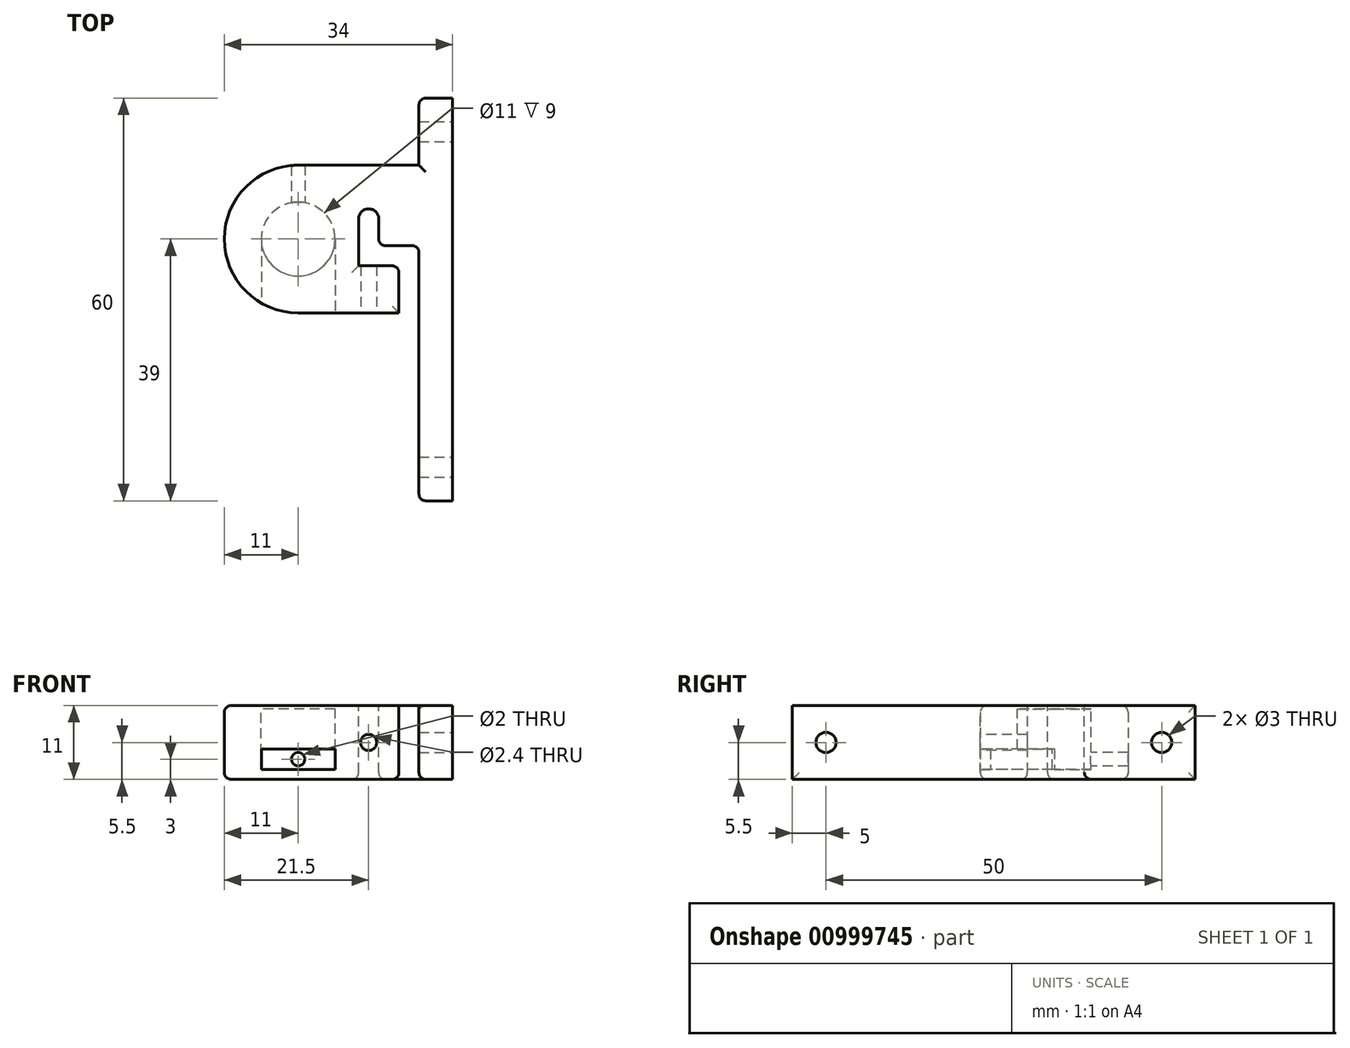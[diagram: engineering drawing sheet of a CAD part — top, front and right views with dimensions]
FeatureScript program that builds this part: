
annotation { "Feature Type Name" : "Feature", "Feature Type Description" : "" }
export const myFeature = defineFeature(function(context is Context, id is Id, definition is map)
    precondition{}
    {
        {
            var Q0;
            Q0=qCreatedBy(makeId("Top.planeOp"),FACE);
            var sketch = newSketch(context, id + "F0", { "sketchPlane" : qUnion([Q0])});
            skArc(sketch, "E0", {"start": v(0, 11) * mm, "mid": v(-11, 0) * mm, "end": v(0, -11) * mm});
            skLineSegment(sketch, "E1.bottom", {"start": v(23, -39) * mm, "end": v(18, -39) * mm});
            skLineSegment(sketch, "E1.top", {"start": v(23, 21) * mm, "end": v(18, 21) * mm});
            skLineSegment(sketch, "E1.left", {"start": v(23, -39) * mm, "end": v(23, 21) * mm});
            skLineSegment(sketch, "E1.right", {"start": v(18, -39) * mm, "end": v(18, -11) * mm});
            skLineSegment(sketch, "E2.bottom", {"start": v(0, 11) * mm, "end": v(18, 11) * mm});
            skLineSegment(sketch, "E2.top", {"start": v(0, -11) * mm, "end": v(18, -11) * mm});
            skLineSegment(sketch, "E3.trimOffspring", {"start": v(18, 11) * mm, "end": v(18, 21) * mm});
            skLineSegment(sketch, "E4", {"start": v(18, 11) * mm, "end": v(18, -11) * mm, "construction": true});
            skSolve(sketch);
        }
        {
            var Q0;
            Q0=qSketchRegion(id+"F0",true);
            extrude(context, id + "F1", {"entities" : qUnion([Q0]), "endBound" : BoundingType.SYMMETRIC, "depth" : 11 * mm, "offsetDistance" : 25 * mm});
        }
        {
            var Q0;
            Q0=makeQuery(id+"F1.opExtrude","SWEPT_FACE",FACE,{"disambiguationData":[OSD([sQuery(id+"F0.wireOp",EDGE,"E1.left")])]});
            var sketch = newSketch(context, id + "F2", { "sketchPlane" : qUnion([Q0])});
            skCircle(sketch, "E5", {"center": v(16, 0) * mm, "radius": 1.5 * mm});
            skCircle(sketch, "E6", {"center": v(-34, 0) * mm, "radius": 1.5 * mm});
            skSolve(sketch);
        }
        {
            var Q0;
            Q0=qSketchRegion(id+"F2",true);
            extrude(context, id + "F3", {"entities" : qUnion([Q0]), "operationType" : NewBodyOperationType.REMOVE, "oppositeDirection" : true, "depth" : 25 * mm, "offsetDistance" : 25 * mm});
        }
        {
            var Q0;
            Q0=makeQuery(id+"F1.opExtrude","CAP_FACE",FACE,{"disambiguationData":[OSD([sQuery(id+"F0.wireOp",EDGE,"E0"),sQuery(id+"F0.wireOp",EDGE,"E1.bottom"),sQuery(id+"F0.wireOp",EDGE,"E1.top"),sQuery(id+"F0.wireOp",EDGE,"E1.left"),sQuery(id+"F0.wireOp",EDGE,"E1.right"),sQuery(id+"F0.wireOp",EDGE,"E2.bottom"),sQuery(id+"F0.wireOp",EDGE,"E2.top"),sQuery(id+"F0.wireOp",EDGE,"E3.trimOffspring")])],"isStart":false});
            var sketch = newSketch(context, id + "F4", { "sketchPlane" : qUnion([Q0])});
            skCircle(sketch, "E7", {"center": v(0, 0) * mm, "radius": 5.5 * mm});
            skSolve(sketch);
        }
        {
            var Q0;
            Q0=makeQuery(id+"F4.imprint","IMPRINT",FACE,{"disambiguationData":[TD([[makeQuery(id+"F4.imprint","IMPRINT",EDGE,{"derivedFrom":sQuery(id+"F4.wireOp",EDGE,"E7")}),1.0]])]});
            extrude(context, id + "F5", {"entities" : qUnion([Q0]), "operationType" : NewBodyOperationType.REMOVE, "oppositeDirection" : true, "depth" : 9.5 * mm, "offsetDistance" : 25 * mm, "hasSecondDirection" : true, "secondDirectionOppositeDirection" : true, "secondDirectionDepth" : .5 * mm});
        }
        {
            var Q0;
            Q0=makeQuery(id+"F1.opExtrude","CAP_FACE",FACE,{"disambiguationData":[OSD([sQuery(id+"F0.wireOp",EDGE,"E0"),sQuery(id+"F0.wireOp",EDGE,"E1.bottom"),sQuery(id+"F0.wireOp",EDGE,"E1.top"),sQuery(id+"F0.wireOp",EDGE,"E1.left"),sQuery(id+"F0.wireOp",EDGE,"E1.right"),sQuery(id+"F0.wireOp",EDGE,"E2.bottom"),sQuery(id+"F0.wireOp",EDGE,"E2.top"),sQuery(id+"F0.wireOp",EDGE,"E3.trimOffspring")])],"isStart":true});
            var sketch = newSketch(context, id + "F6", { "sketchPlane" : qUnion([Q0])});
            skLineSegment(sketch, "E8.bottom", {"start": v(-5.5, 0) * mm, "end": v(5.5, 0) * mm});
            skLineSegment(sketch, "E8.top", {"start": v(-5.5, 16.46) * mm, "end": v(5.5, 16.46) * mm});
            skLineSegment(sketch, "E8.left", {"start": v(-5.5, 0) * mm, "end": v(-5.5, 16.46) * mm});
            skLineSegment(sketch, "E8.right", {"start": v(5.5, 0) * mm, "end": v(5.5, 16.46) * mm});
            skSolve(sketch);
        }
        {
            var Q0;
            Q0=qSketchRegion(id+"F6",true);
            extrude(context, id + "F7", {"entities" : qUnion([Q0]), "operationType" : NewBodyOperationType.REMOVE, "oppositeDirection" : true, "depth" : 4.5 * mm, "offsetDistance" : 25 * mm, "hasSecondDirection" : true, "secondDirectionOppositeDirection" : true, "secondDirectionDepth" : 1.5 * mm});
        }
        {
            var Q0;
            Q0=makeQuery(id+"F1.opExtrude","SWEPT_FACE",FACE,{"disambiguationData":[OSD([sQuery(id+"F0.wireOp",EDGE,"E2.top")])]});
            var sketch = newSketch(context, id + "F8", { "sketchPlane" : qUnion([Q0])});
            skCircle(sketch, "E9", {"center": v(0, -2.5) * mm, "radius": 1 * mm});
            skPoint(sketch, "E9.centerSnap0", {"position": v(5.5, -2.5) * mm});
            skSolve(sketch);
        }
        {
            var Q0;
            Q0=qSketchRegion(id+"F8",true);
            extrude(context, id + "F9", {"entities" : qUnion([Q0]), "operationType" : NewBodyOperationType.REMOVE, "oppositeDirection" : true, "depth" : 25 * mm, "offsetDistance" : 25 * mm});
        }
        {
            var Q0;
            Q0=makeQuery(id+"F4.imprint","IMPRINT",FACE,{"disambiguationData":[TD([[makeQuery(id+"F4.imprint","IMPRINT",EDGE,{"derivedFrom":sQuery(id+"F4.wireOp",EDGE,"E7")}),-1.0]])]});
            var sketch = newSketch(context, id + "F10", { "sketchPlane" : qUnion([Q0])});
            skArc(sketch, "E10", {"start": v(12, 3) * mm, "mid": v(10.5, 4.5) * mm, "end": v(9, 3) * mm});
            skLineSegment(sketch, "E11", {"start": v(9, 3) * mm, "end": v(9, -4) * mm});
            skLineSegment(sketch, "E12", {"start": v(9, -4) * mm, "end": v(15, -4) * mm});
            skLineSegment(sketch, "E13", {"start": v(15, -4) * mm, "end": v(15, -11) * mm});
            skLineSegment(sketch, "E14", {"start": v(15, -11) * mm, "end": v(18, -11) * mm});
            skLineSegment(sketch, "E15", {"start": v(18, -11) * mm, "end": v(18, -1) * mm});
            skLineSegment(sketch, "E16", {"start": v(18, -1) * mm, "end": v(12, -1) * mm});
            skLineSegment(sketch, "E17", {"start": v(12, -1) * mm, "end": v(12, 3) * mm});
            skSolve(sketch);
        }
        {
            var Q0;
            Q0=qSketchRegion(id+"F10",true);
            extrude(context, id + "F11", {"entities" : qUnion([Q0]), "operationType" : NewBodyOperationType.REMOVE, "oppositeDirection" : true, "depth" : 25 * mm, "offsetDistance" : 25 * mm});
        }
        {
            var Q0;
            Q0=makeQuery(id+"F1.opExtrude","SWEPT_FACE",FACE,{"disambiguationData":[OSD([sQuery(id+"F0.wireOp",EDGE,"E2.top")])]});
            var sketch = newSketch(context, id + "F12", { "sketchPlane" : qUnion([Q0])});
            skCircle(sketch, "E18", {"center": v(10.5, 0) * mm, "radius": 1.2 * mm});
            skSolve(sketch);
        }
        {
            var Q0;
            Q0=qSketchRegion(id+"F12",true);
            extrude(context, id + "F13", {"entities" : qUnion([Q0]), "operationType" : NewBodyOperationType.REMOVE, "endBound" : BoundingType.UP_TO_NEXT, "oppositeDirection" : true, "depth" : 25 * mm, "offsetDistance" : 25 * mm});
        }
        {
            var Q0;
            Q0=makeQuery(id+"F1.opExtrude","CAP_EDGE",EDGE,{"disambiguationData":[OSD([sQuery(id+"F0.wireOp",EDGE,"E3.trimOffspring")])],"isStart":false});
            var Q1;
            Q1=makeQuery(id+"F1.opExtrude","SWEPT_EDGE",EDGE,{"disambiguationData":[OSD([sQuery(id+"F0.wireOp",EDGE,"E1.top"),sQuery(id+"F0.wireOp",EDGE,"E3.trimOffspring")])]});
            var Q2;
            Q2=makeQuery(id+"F1.opExtrude","CAP_EDGE",EDGE,{"disambiguationData":[OSD([sQuery(id+"F0.wireOp",EDGE,"E3.trimOffspring")])],"isStart":true});
            var Q3;
            Q3=makeQuery(id+"F1.opExtrude","CAP_EDGE",EDGE,{"disambiguationData":[OSD([sQuery(id+"F0.wireOp",EDGE,"E2.bottom")])],"isStart":false});
            var Q4;
            Q4=makeQuery(id+"F11.boolean.opBoolean","MERGE",EDGE,{"derivedFrom":[makeQuery(id+"F1.opExtrude","CAP_EDGE",EDGE,{"disambiguationData":[OSD([sQuery(id+"F0.wireOp",EDGE,"E1.right")])],"isStart":false})],"fromTools":[makeQuery(id+"F11.opExtrude","CAP_EDGE",EDGE,{"disambiguationData":[OSD([sQuery(id+"F10.wireOp",EDGE,"E15")])],"isStart":true})]});
            var Q5;
            Q5=makeQuery(id+"F1.opExtrude","CAP_EDGE",EDGE,{"disambiguationData":[OSD([sQuery(id+"F0.wireOp",EDGE,"E0")])],"isStart":true});
            var Q6;
            Q6=makeQuery(id+"F1.opExtrude","CAP_EDGE",EDGE,{"disambiguationData":[OSD([sQuery(id+"F0.wireOp",EDGE,"E2.top")])],"isStart":true});
            var Q7;
            Q7=makeQuery(id+"F11.boolean.opBoolean","INTERSECT",EDGE,{"derivedFrom":[makeQuery(id+"F1.opExtrude","CAP_FACE",FACE,{"disambiguationData":[OSD([sQuery(id+"F0.wireOp",EDGE,"E0"),sQuery(id+"F0.wireOp",EDGE,"E1.bottom"),sQuery(id+"F0.wireOp",EDGE,"E1.top"),sQuery(id+"F0.wireOp",EDGE,"E1.left"),sQuery(id+"F0.wireOp",EDGE,"E1.right"),sQuery(id+"F0.wireOp",EDGE,"E2.bottom"),sQuery(id+"F0.wireOp",EDGE,"E2.top"),sQuery(id+"F0.wireOp",EDGE,"E3.trimOffspring")])],"isStart":true}),makeQuery(id+"F11.opExtrude","SWEPT_FACE",FACE,{"disambiguationData":[OSD([sQuery(id+"F10.wireOp",EDGE,"E15")])]})]});
            var Q8;
            Q8=makeQuery(id+"F11.boolean.opBoolean","INTERSECT",EDGE,{"derivedFrom":[makeQuery(id+"F1.opExtrude","CAP_FACE",FACE,{"disambiguationData":[OSD([sQuery(id+"F0.wireOp",EDGE,"E0"),sQuery(id+"F0.wireOp",EDGE,"E1.bottom"),sQuery(id+"F0.wireOp",EDGE,"E1.top"),sQuery(id+"F0.wireOp",EDGE,"E1.left"),sQuery(id+"F0.wireOp",EDGE,"E1.right"),sQuery(id+"F0.wireOp",EDGE,"E2.bottom"),sQuery(id+"F0.wireOp",EDGE,"E2.top"),sQuery(id+"F0.wireOp",EDGE,"E3.trimOffspring")])],"isStart":true}),makeQuery(id+"F11.opExtrude","SWEPT_FACE",FACE,{"disambiguationData":[OSD([sQuery(id+"F10.wireOp",EDGE,"E16")])]})]});
            var Q9;
            Q9=makeQuery(id+"F1.opExtrude","SWEPT_EDGE",EDGE,{"disambiguationData":[OSD([sQuery(id+"F0.wireOp",EDGE,"E1.bottom"),sQuery(id+"F0.wireOp",EDGE,"E1.right")])]});
            var Q10;
            Q10=makeQuery(id+"F11.boolean.opBoolean","COPY",EDGE,{"derivedFrom":makeQuery(id+"F11.opExtrude","SWEPT_EDGE",EDGE,{"disambiguationData":[OSD([sQuery(id+"F10.wireOp",EDGE,"E15"),sQuery(id+"F10.wireOp",EDGE,"E16")])]})});
            var Q11;
            Q11=makeQuery(id+"F11.boolean.opBoolean","COPY",EDGE,{"derivedFrom":makeQuery(id+"F11.opExtrude","CAP_EDGE",EDGE,{"disambiguationData":[OSD([sQuery(id+"F10.wireOp",EDGE,"E17")])],"isStart":true})});
            var Q12;
            Q12=makeQuery(id+"F11.boolean.opBoolean","COPY",EDGE,{"derivedFrom":makeQuery(id+"F11.opExtrude","CAP_EDGE",EDGE,{"disambiguationData":[OSD([sQuery(id+"F10.wireOp",EDGE,"E12")])],"isStart":true})});
            var Q13;
            Q13=makeQuery(id+"F11.boolean.opBoolean","INTERSECT",EDGE,{"derivedFrom":[makeQuery(id+"F1.opExtrude","CAP_FACE",FACE,{"disambiguationData":[OSD([sQuery(id+"F0.wireOp",EDGE,"E0"),sQuery(id+"F0.wireOp",EDGE,"E1.bottom"),sQuery(id+"F0.wireOp",EDGE,"E1.top"),sQuery(id+"F0.wireOp",EDGE,"E1.left"),sQuery(id+"F0.wireOp",EDGE,"E1.right"),sQuery(id+"F0.wireOp",EDGE,"E2.bottom"),sQuery(id+"F0.wireOp",EDGE,"E2.top"),sQuery(id+"F0.wireOp",EDGE,"E3.trimOffspring")])],"isStart":true}),makeQuery(id+"F11.opExtrude","SWEPT_FACE",FACE,{"disambiguationData":[OSD([sQuery(id+"F10.wireOp",EDGE,"E13")])]})]});
            var Q14;
            Q14=makeQuery(id+"F11.boolean.opBoolean","COPY",EDGE,{"derivedFrom":makeQuery(id+"F11.opExtrude","CAP_EDGE",EDGE,{"disambiguationData":[OSD([sQuery(id+"F10.wireOp",EDGE,"E13")])],"isStart":true})});
            var Q15;
            Q15=makeQuery(id+"F11.boolean.opBoolean","COPY",EDGE,{"derivedFrom":makeQuery(id+"F11.opExtrude","SWEPT_EDGE",EDGE,{"disambiguationData":[OSD([sQuery(id+"F0.wireOp",EDGE,"E2.top"),sQuery(id+"F10.wireOp",EDGE,"E13"),sQuery(id+"F10.wireOp",EDGE,"E14")])]})});
            var Q16;
            Q16=makeQuery(id+"F11.boolean.opBoolean","COPY",EDGE,{"derivedFrom":makeQuery(id+"F11.opExtrude","SWEPT_EDGE",EDGE,{"disambiguationData":[OSD([sQuery(id+"F10.wireOp",EDGE,"E12"),sQuery(id+"F10.wireOp",EDGE,"E13")])]})});
            var Q17;
            Q17=makeQuery(id+"F11.boolean.opBoolean","COPY",EDGE,{"derivedFrom":makeQuery(id+"F11.opExtrude","SWEPT_EDGE",EDGE,{"disambiguationData":[OSD([sQuery(id+"F10.wireOp",EDGE,"E16"),sQuery(id+"F10.wireOp",EDGE,"E17")])]})});
            var Q18;
            Q18=makeQuery(id+"F11.boolean.opBoolean","INTERSECT",EDGE,{"derivedFrom":[makeQuery(id+"F1.opExtrude","CAP_FACE",FACE,{"disambiguationData":[OSD([sQuery(id+"F0.wireOp",EDGE,"E0"),sQuery(id+"F0.wireOp",EDGE,"E1.bottom"),sQuery(id+"F0.wireOp",EDGE,"E1.top"),sQuery(id+"F0.wireOp",EDGE,"E1.left"),sQuery(id+"F0.wireOp",EDGE,"E1.right"),sQuery(id+"F0.wireOp",EDGE,"E2.bottom"),sQuery(id+"F0.wireOp",EDGE,"E2.top"),sQuery(id+"F0.wireOp",EDGE,"E3.trimOffspring")])],"isStart":true}),makeQuery(id+"F11.opExtrude","SWEPT_FACE",FACE,{"disambiguationData":[OSD([sQuery(id+"F10.wireOp",EDGE,"E11")])]})]});
            var Q19;
            Q19=makeQuery(id+"F11.boolean.opBoolean","INTERSECT",EDGE,{"derivedFrom":[makeQuery(id+"F1.opExtrude","CAP_FACE",FACE,{"disambiguationData":[OSD([sQuery(id+"F0.wireOp",EDGE,"E0"),sQuery(id+"F0.wireOp",EDGE,"E1.bottom"),sQuery(id+"F0.wireOp",EDGE,"E1.top"),sQuery(id+"F0.wireOp",EDGE,"E1.left"),sQuery(id+"F0.wireOp",EDGE,"E1.right"),sQuery(id+"F0.wireOp",EDGE,"E2.bottom"),sQuery(id+"F0.wireOp",EDGE,"E2.top"),sQuery(id+"F0.wireOp",EDGE,"E3.trimOffspring")])],"isStart":true}),makeQuery(id+"F11.opExtrude","SWEPT_FACE",FACE,{"disambiguationData":[OSD([sQuery(id+"F10.wireOp",EDGE,"E12")])]})]});
            fillet(context, id + "F14", {"entities" : qUnion([Q0, Q1, Q2, Q3, Q4, Q5, Q6, Q7, Q8, Q9, Q10, Q11, Q12, Q13, Q14, Q15, Q16, Q17, Q18, Q19]), "radius" : 1 * mm, "tangentPropagation" : true, "allowEdgeOverflow" : false});
        }
    });
